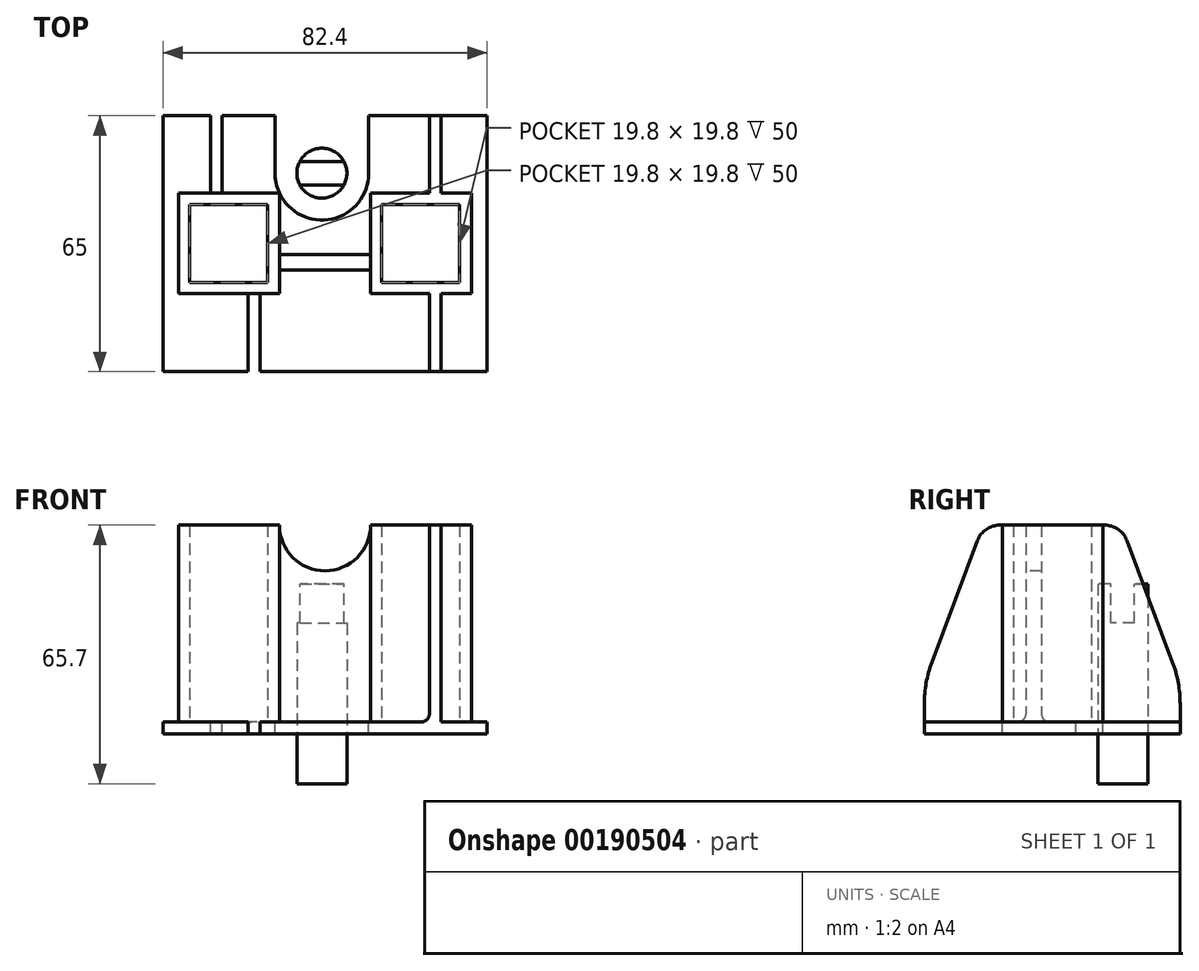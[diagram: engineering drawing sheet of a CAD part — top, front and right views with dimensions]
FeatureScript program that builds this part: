
annotation { "Feature Type Name" : "Feature", "Feature Type Description" : "" }
export const myFeature = defineFeature(function(context is Context, id is Id, definition is map)
    precondition{}
    {
        {
            var Q0;
            Q0=qCreatedBy(makeId("Top.planeOp"),FACE);
            var sketch = newSketch(context, id + "F0", { "sketchPlane" : qUnion([Q0])});
            skLineSegment(sketch, "E0.bottom", {"start": v(-33.6, -8) * mm, "end": v(-13.8, -8) * mm});
            skLineSegment(sketch, "E0.top", {"start": v(-33.6, -27.8) * mm, "end": v(-13.8, -27.8) * mm});
            skLineSegment(sketch, "E0.left", {"start": v(-33.6, -8) * mm, "end": v(-33.6, -27.8) * mm});
            skLineSegment(sketch, "E0.right", {"start": v(-13.8, -8) * mm, "end": v(-13.8, -27.8) * mm});
            skLineSegment(sketch, "E1.bottom", {"start": v(-36.4, -5) * mm, "end": v(-10.8, -5) * mm});
            skLineSegment(sketch, "E1.top", {"start": v(-36.4, -30.6) * mm, "end": v(-10.8, -30.6) * mm});
            skLineSegment(sketch, "E1.left", {"start": v(-36.4, -5) * mm, "end": v(-36.4, -30.6) * mm});
            skLineSegment(sketch, "E1.right", {"start": v(-10.8, -5) * mm, "end": v(-10.8, -30.6) * mm});
            skCircle(sketch, "E2", {"center": v(0, 0) * mm, "radius": 6.35 * mm});
            skLineSegment(sketch, "E3.bottom", {"start": v(15.2, -8) * mm, "end": v(35, -8) * mm});
            skLineSegment(sketch, "E3.top", {"start": v(15.2, -27.8) * mm, "end": v(35, -27.8) * mm});
            skLineSegment(sketch, "E3.left", {"start": v(15.2, -8) * mm, "end": v(15.2, -27.8) * mm});
            skLineSegment(sketch, "E3.right", {"start": v(35, -8) * mm, "end": v(35, -27.8) * mm});
            skLineSegment(sketch, "E4.bottom", {"start": v(12.4, -5) * mm, "end": v(38, -5) * mm});
            skLineSegment(sketch, "E4.top", {"start": v(12.4, -30.6) * mm, "end": v(38, -30.6) * mm});
            skLineSegment(sketch, "E4.left", {"start": v(12.4, -5) * mm, "end": v(12.4, -30.6) * mm});
            skLineSegment(sketch, "E4.right", {"start": v(38, -5) * mm, "end": v(38, -30.6) * mm});
            skLineSegment(sketch, "E5.bottom", {"start": v(42, -50.4) * mm, "end": v(0.8, -50.4) * mm});
            skLineSegment(sketch, "E5.top", {"start": v(42, 14.6) * mm, "end": v(11.9, 14.6) * mm});
            skLineSegment(sketch, "E5.left", {"start": v(42, -50.4) * mm, "end": v(42, 14.6) * mm});
            skLineSegment(sketch, "E5.right", {"start": v(-40.4, -50.4) * mm, "end": v(-40.4, 14.6) * mm});
            skLineSegment(sketch, "E6", {"start": v(9.6, -50.4) * mm, "end": v(-40.4, -50.4) * mm});
            skLineSegment(sketch, "E7", {"start": v(-36.4, -5) * mm, "end": v(-34.4, -5) * mm});
            skArc(sketch, "E8", {"start": v(-11.9, 0) * mm, "mid": v(0, -11.9) * mm, "end": v(11.9, 0) * mm});
            skLineSegment(sketch, "E9", {"start": v(-11.9, 0) * mm, "end": v(-11.9, 14.6) * mm});
            skLineSegment(sketch, "E10", {"start": v(11.9, 0) * mm, "end": v(11.9, 14.6) * mm});
            skLineSegment(sketch, "E11", {"start": v(-11.9, 14.6) * mm, "end": v(-40.4, 14.6) * mm});
            skLineSegment(sketch, "E12.bottom", {"start": v(-18.7, -50.4) * mm, "end": v(-15.7, -50.4) * mm});
            skLineSegment(sketch, "E12.top", {"start": v(-18.7, -30.6) * mm, "end": v(-15.7, -30.6) * mm});
            skLineSegment(sketch, "E12.left", {"start": v(-18.7, -50.4) * mm, "end": v(-18.7, -30.6) * mm});
            skLineSegment(sketch, "E12.right", {"start": v(-15.7, -50.4) * mm, "end": v(-15.7, -30.6) * mm});
            skLineSegment(sketch, "E13.bottom", {"start": v(-28.3, -5) * mm, "end": v(-25.3, -5) * mm});
            skLineSegment(sketch, "E13.top", {"start": v(-28.3, 14.6) * mm, "end": v(-25.3, 14.6) * mm});
            skLineSegment(sketch, "E13.left", {"start": v(-28.3, -5) * mm, "end": v(-28.3, 14.6) * mm});
            skLineSegment(sketch, "E13.right", {"start": v(-25.3, -5) * mm, "end": v(-25.3, 14.6) * mm});
            skLineSegment(sketch, "E14.bottom", {"start": v(-10.8, -20.6) * mm, "end": v(12.4, -20.6) * mm});
            skLineSegment(sketch, "E14.top", {"start": v(-10.8, -24.6) * mm, "end": v(12.4, -24.6) * mm});
            skLineSegment(sketch, "E14.left", {"start": v(-10.8, -20.6) * mm, "end": v(-10.8, -24.6) * mm});
            skLineSegment(sketch, "E14.right", {"start": v(12.4, -20.6) * mm, "end": v(12.4, -24.6) * mm});
            skLineSegment(sketch, "E15.MirrorCS", {"start": v(27.3, -50.4) * mm, "end": v(27.3, -30.6) * mm});
            skLineSegment(sketch, "E16.MirrorCS", {"start": v(30.3, -50.4) * mm, "end": v(30.3, -30.6) * mm});
            skLineSegment(sketch, "E17.MirrorCS", {"start": v(27.3, -5) * mm, "end": v(27.3, 14.6) * mm});
            skLineSegment(sketch, "E18.MirrorCS", {"start": v(30.3, -5) * mm, "end": v(30.3, 14.6) * mm});
            skSolve(sketch);
        }
        {
            var Q0;
            Q0=makeQuery(id+"F0.imprint","IMPRINT",FACE,{"disambiguationData":[TD([[makeQuery(id+"F0.imprint","IMPRINT",EDGE,{"derivedFrom":sQuery(id+"F0.wireOp",EDGE,"E2")}),1.0]])]});
            extrude(context, id + "F1", {"entities" : qUnion([Q0]), "depth" : 50.8 * mm});
        }
        {
            var Q0;
            Q0=makeQuery(id+"F1.opExtrude","CAP_FACE",FACE,{"disambiguationData":[OSD([sQuery(id+"F0.wireOp",EDGE,"E2")])],"isStart":false});
            var sketch = newSketch(context, id + "F2", { "sketchPlane" : qUnion([Q0])});
            skLineSegment(sketch, "E19.bottom", {"start": v(-7.56, 3) * mm, "end": v(-7.56, -3) * mm});
            skLineSegment(sketch, "E19.top", {"start": v(7.56, 3) * mm, "end": v(7.56, -3) * mm});
            skLineSegment(sketch, "E19.left", {"start": v(-7.56, 3) * mm, "end": v(7.56, 3) * mm});
            skLineSegment(sketch, "E19.right", {"start": v(-7.56, -3) * mm, "end": v(7.56, -3) * mm});
            skPoint(sketch, "E19.middle", {"position": v(0, 0) * mm});
            skSolve(sketch);
        }
        {
            var Q0;
            {var subQ0=sQuery(id+"F2.wireOp",EDGE,"E19.left");var subQ1=makeQuery(id+"F1.opExtrude","CAP_EDGE",EDGE,{"disambiguationData":[OSD([sQuery(id+"F0.wireOp",EDGE,"E2")])],"isStart":false});var subQ2=makeQuery(id+"F2.imprint","INTERSECT",VERTEX,{"disambiguationData":[OD(0.0)],"derivedFrom":[subQ1,subQ0]});Q0=makeQuery(id+"F2.imprint","IMPRINT",FACE,{"disambiguationData":[TD([[makeQuery(id+"F2.imprint","IMPRINT",EDGE,{"disambiguationData":[TD([[subQ2,-1.0]])],"derivedFrom":subQ0}),-1.0]])]});}
            extrude(context, id + "F3", {"entities" : qUnion([Q0]), "operationType" : NewBodyOperationType.REMOVE, "oppositeDirection" : true, "depth" : 10 * mm});
        }
        {
            var Q0;
            Q0=makeQuery(id+"F1.opExtrude","SWEPT_BODY",BODY,{"disambiguationData":[OSD([sQuery(id+"F0.wireOp",EDGE,"E2")])]});
            transform(context, id + "F4", {"entities" : qUnion([Q0]), "transformType" : TransformType.TRANSLATION_3D, "dx" : 0 * mm, "dy" : 0 * mm, "dz" : -15.7 * mm, "makeCopy" : false});
        }
        {
            var Q0;
            {var subQ1=sQuery(id+"F0.wireOp",EDGE,"E1.left");Q0=makeQuery(id+"F0.imprint","IMPRINT",FACE,{"disambiguationData":[TD([[makeQuery(id+"F0.imprint","IMPRINT",EDGE,{"derivedFrom":subQ1}),-1.0]])]});}
            var Q1;
            Q1=makeQuery(id+"F0.imprint","IMPRINT",FACE,{"disambiguationData":[TD([[makeQuery(id+"F0.imprint","IMPRINT",EDGE,{"derivedFrom":sQuery(id+"F0.wireOp",EDGE,"E13.bottom")}),1.0]])]});
            var Q2;
            Q2=makeQuery(id+"F0.imprint","IMPRINT",FACE,{"disambiguationData":[TD([[makeQuery(id+"F0.imprint","IMPRINT",EDGE,{"derivedFrom":sQuery(id+"F0.wireOp",EDGE,"E0.bottom")}),1.0]])]});
            var Q3;
            Q3=makeQuery(id+"F0.imprint","IMPRINT",FACE,{"disambiguationData":[TD([[makeQuery(id+"F0.imprint","IMPRINT",EDGE,{"derivedFrom":sQuery(id+"F0.wireOp",EDGE,"E0.bottom")}),-1.0]])]});
            var Q4;
            {var subQ1=sQuery(id+"F0.wireOp",EDGE,"E9");Q4=makeQuery(id+"F0.imprint","IMPRINT",FACE,{"disambiguationData":[TD([[makeQuery(id+"F0.imprint","IMPRINT",EDGE,{"derivedFrom":subQ1}),1.0]])]});}
            var Q5;
            {var subQ0=sQuery(id+"F0.wireOp",EDGE,"E10");Q5=makeQuery(id+"F0.imprint","IMPRINT",FACE,{"disambiguationData":[TD([[makeQuery(id+"F0.imprint","IMPRINT",EDGE,{"derivedFrom":subQ0}),-1.0]])]});}
            var Q6;
            Q6=makeQuery(id+"F0.imprint","IMPRINT",FACE,{"disambiguationData":[TD([[makeQuery(id+"F0.imprint","IMPRINT",EDGE,{"derivedFrom":sQuery(id+"F0.wireOp",EDGE,"E14.bottom")}),-1.0]])]});
            var Q7;
            Q7=makeQuery(id+"F0.imprint","IMPRINT",FACE,{"disambiguationData":[TD([[makeQuery(id+"F0.imprint","IMPRINT",EDGE,{"derivedFrom":sQuery(id+"F0.wireOp",EDGE,"E12.bottom")}),1.0]])]});
            var Q8;
            {var subQ7=sQuery(id+"F0.wireOp",EDGE,"E12.right");Q8=makeQuery(id+"F0.imprint","IMPRINT",FACE,{"disambiguationData":[TD([[makeQuery(id+"F0.imprint","IMPRINT",EDGE,{"derivedFrom":subQ7}),-1.0]])]});}
            var Q9;
            Q9=makeQuery(id+"F0.imprint","IMPRINT",FACE,{"disambiguationData":[TD([[makeQuery(id+"F0.imprint","IMPRINT",EDGE,{"derivedFrom":sQuery(id+"F0.wireOp",EDGE,"E3.bottom")}),1.0]])]});
            var Q10;
            {var subQ0=sQuery(id+"F0.wireOp",EDGE,"E17.MirrorCS");Q10=makeQuery(id+"F0.imprint","IMPRINT",FACE,{"disambiguationData":[TD([[makeQuery(id+"F0.imprint","IMPRINT",EDGE,{"derivedFrom":subQ0}),-1.0]])]});}
            var Q11;
            {var subQ3=sQuery(id+"F0.wireOp",EDGE,"E4.right");Q11=makeQuery(id+"F0.imprint","IMPRINT",FACE,{"disambiguationData":[TD([[makeQuery(id+"F0.imprint","IMPRINT",EDGE,{"derivedFrom":subQ3}),1.0]])]});}
            var Q12;
            {var subQ0=sQuery(id+"F0.wireOp",EDGE,"E15.MirrorCS");Q12=makeQuery(id+"F0.imprint","IMPRINT",FACE,{"disambiguationData":[TD([[makeQuery(id+"F0.imprint","IMPRINT",EDGE,{"derivedFrom":subQ0}),-1.0]])]});}
            var Q13;
            Q13=makeQuery(id+"F0.imprint","IMPRINT",FACE,{"disambiguationData":[TD([[makeQuery(id+"F0.imprint","IMPRINT",EDGE,{"derivedFrom":sQuery(id+"F0.wireOp",EDGE,"E3.bottom")}),-1.0]])]});
            extrude(context, id + "F5", {"entities" : qUnion([Q0, Q1, Q2, Q3, Q4, Q5, Q6, Q7, Q8, Q9, Q10, Q11, Q12, Q13]), "oppositeDirection" : true, "depth" : 3 * mm});
        }
        {
            var Q0;
            Q0=makeQuery(id+"F0.imprint","IMPRINT",FACE,{"disambiguationData":[TD([[makeQuery(id+"F0.imprint","IMPRINT",EDGE,{"derivedFrom":sQuery(id+"F0.wireOp",EDGE,"E0.bottom")}),1.0]])]});
            var Q1;
            Q1=makeQuery(id+"F0.imprint","IMPRINT",FACE,{"disambiguationData":[TD([[makeQuery(id+"F0.imprint","IMPRINT",EDGE,{"derivedFrom":sQuery(id+"F0.wireOp",EDGE,"E3.bottom")}),1.0]])]});
            var Q2;
            Q2=makeQuery(id+"F0.imprint","IMPRINT",FACE,{"disambiguationData":[TD([[makeQuery(id+"F0.imprint","IMPRINT",EDGE,{"derivedFrom":sQuery(id+"F0.wireOp",EDGE,"E14.bottom")}),-1.0]])]});
            var Q3;
            Q3=makeQuery(id+"F0.imprint","IMPRINT",FACE,{"disambiguationData":[TD([[makeQuery(id+"F0.imprint","IMPRINT",EDGE,{"derivedFrom":sQuery(id+"F0.wireOp",EDGE,"E12.bottom")}),1.0]])]});
            var Q4;
            {var subQ0=sQuery(id+"F0.wireOp",EDGE,"E15.MirrorCS");Q4=makeQuery(id+"F0.imprint","IMPRINT",FACE,{"disambiguationData":[TD([[makeQuery(id+"F0.imprint","IMPRINT",EDGE,{"derivedFrom":subQ0}),-1.0]])]});}
            var Q5;
            Q5=makeQuery(id+"F0.imprint","IMPRINT",FACE,{"disambiguationData":[TD([[makeQuery(id+"F0.imprint","IMPRINT",EDGE,{"derivedFrom":sQuery(id+"F0.wireOp",EDGE,"E13.bottom")}),1.0]])]});
            var Q6;
            {var subQ0=sQuery(id+"F0.wireOp",EDGE,"E17.MirrorCS");Q6=makeQuery(id+"F0.imprint","IMPRINT",FACE,{"disambiguationData":[TD([[makeQuery(id+"F0.imprint","IMPRINT",EDGE,{"derivedFrom":subQ0}),-1.0]])]});}
            extrude(context, id + "F6", {"entities" : qUnion([Q0, Q1, Q2, Q3, Q4, Q5, Q6]), "operationType" : NewBodyOperationType.ADD, "depth" : 50 * mm});
        }
        {
            var Q0;
            Q0=makeQuery(id+"F6.opExtrude","SWEPT_FACE",FACE,{"disambiguationData":[OSD([sQuery(id+"F0.wireOp",EDGE,"E14.top")])]});
            var sketch = newSketch(context, id + "F7", { "sketchPlane" : qUnion([Q0])});
            skCircle(sketch, "E20", {"center": v(0.8, 50) * mm, "radius": 11.6 * mm});
            skSolve(sketch);
        }
        {
            var Q0;
            {var subQ1=sQuery(id+"F0.wireOp",EDGE,"E14.top");var subQ2=makeQuery(id+"F6.opExtrude","CAP_EDGE",EDGE,{"disambiguationData":[OSD([subQ1])],"isStart":false});Q0=makeQuery(id+"F7.imprint","IMPRINT",FACE,{"disambiguationData":[TD([[makeQuery(id+"F7.imprint","IMPRINT",EDGE,{"derivedFrom":subQ2}),-1.0]])]});}
            extrude(context, id + "F8", {"entities" : qUnion([Q0]), "operationType" : NewBodyOperationType.REMOVE, "oppositeDirection" : true, "depth" : 4 * mm});
        }
        {
            var Q0;
            Q0=makeQuery(id+"F6.opExtrude","CAP_EDGE",EDGE,{"disambiguationData":[OSD([sQuery(id+"F0.wireOp",EDGE,"E5.bottom")])],"isStart":false});
            var Q1;
            Q1=makeQuery(id+"F6.opExtrude","CAP_EDGE",EDGE,{"disambiguationData":[OSD([sQuery(id+"F0.wireOp",EDGE,"E12.bottom")])],"isStart":false});
            var Q2;
            Q2=makeQuery(id+"F6.opExtrude","CAP_EDGE",EDGE,{"disambiguationData":[OSD([sQuery(id+"F0.wireOp",EDGE,"E5.top")])],"isStart":false});
            var Q3;
            Q3=makeQuery(id+"F6.opExtrude","CAP_EDGE",EDGE,{"disambiguationData":[OSD([sQuery(id+"F0.wireOp",EDGE,"E13.top")])],"isStart":false});
            chamfer(context, id + "F9", {"entities" : qUnion([Q0, Q1, Q2, Q3]), "chamferType" : ChamferType.TWO_OFFSETS, "width1" : 40 * mm, "oppositeDirection" : false, "width2" : 15 * mm, "tangentPropagation" : true});
        }
        {
            var Q0;
            {var subQ0=sQuery(id+"F0.wireOp",EDGE,"E14.top");var subQ1=sQuery(id+"F0.wireOp",EDGE,"E13.right");var subQ2=sQuery(id+"F0.wireOp",EDGE,"E13.left");var subQ3=sQuery(id+"F0.wireOp",EDGE,"E5.bottom");var subQ4=sQuery(id+"F0.wireOp",EDGE,"E13.top");var subQ5=sQuery(id+"F0.wireOp",EDGE,"E12.right");var subQ6=sQuery(id+"F0.wireOp",EDGE,"E12.left");var subQ7=sQuery(id+"F0.wireOp",EDGE,"E14.bottom");var subQ8=sQuery(id+"F0.wireOp",EDGE,"E12.bottom");var subQ9=sQuery(id+"F0.wireOp",EDGE,"E1.right");var subQ10=sQuery(id+"F0.wireOp",EDGE,"E1.bottom");var subQ12=sQuery(id+"F0.wireOp",EDGE,"E0.right");var subQ13=sQuery(id+"F0.wireOp",EDGE,"E1.left");var subQ14=sQuery(id+"F0.wireOp",EDGE,"E0.left");var subQ15=sQuery(id+"F0.wireOp",EDGE,"E1.top");var subQ17=sQuery(id+"F0.wireOp",EDGE,"E0.top");var subQ18=sQuery(id+"F0.wireOp",EDGE,"E0.bottom");var subQ19=sQuery(id+"F0.wireOp",EDGE,"E7");Q0=makeQuery(id+"F9.opChamfer","BLEND_EDGE",EDGE,{"blendedFrom":[makeQuery(id+"F6.opExtrude","CAP_EDGE",EDGE,{"disambiguationData":[OSD([subQ8])],"isStart":false}),makeQuery(id+"F8.boolean.opBoolean","SPLIT",FACE,{"disambiguationData":[TD([makeQuery(id+"F6.opExtrude","SWEPT_FACE",FACE,{"disambiguationData":[OSD([subQ18])]})])],"derivedFrom":makeQuery(id+"F6.opExtrude","CAP_FACE",FACE,{"disambiguationData":[OSD([subQ18,subQ17,subQ14,subQ12,subQ10,subQ15,subQ13,subQ9,sQuery(id+"F0.wireOp",EDGE,"E3.bottom"),sQuery(id+"F0.wireOp",EDGE,"E3.top"),sQuery(id+"F0.wireOp",EDGE,"E3.left"),sQuery(id+"F0.wireOp",EDGE,"E3.right"),sQuery(id+"F0.wireOp",EDGE,"E4.bottom"),sQuery(id+"F0.wireOp",EDGE,"E4.top"),sQuery(id+"F0.wireOp",EDGE,"E4.left"),sQuery(id+"F0.wireOp",EDGE,"E4.right"),subQ3,sQuery(id+"F0.wireOp",EDGE,"E5.top"),subQ19,subQ8,subQ6,subQ5,subQ4,subQ2,subQ1,subQ7,subQ0,sQuery(id+"F0.wireOp",EDGE,"E15.MirrorCS"),sQuery(id+"F0.wireOp",EDGE,"E16.MirrorCS"),sQuery(id+"F0.wireOp",EDGE,"E17.MirrorCS"),sQuery(id+"F0.wireOp",EDGE,"E18.MirrorCS")])],"isStart":false})})],"blendedInto":[makeQuery(id+"F8.boolean.opBoolean","SPLIT",FACE,{"disambiguationData":[TD([makeQuery(id+"F6.opExtrude","SWEPT_FACE",FACE,{"disambiguationData":[OSD([subQ18])]})])],"derivedFrom":makeQuery(id+"F6.opExtrude","CAP_FACE",FACE,{"disambiguationData":[OSD([subQ18,subQ17,subQ14,subQ12,subQ10,subQ15,subQ13,subQ9,sQuery(id+"F0.wireOp",EDGE,"E3.bottom"),sQuery(id+"F0.wireOp",EDGE,"E3.top"),sQuery(id+"F0.wireOp",EDGE,"E3.left"),sQuery(id+"F0.wireOp",EDGE,"E3.right"),sQuery(id+"F0.wireOp",EDGE,"E4.bottom"),sQuery(id+"F0.wireOp",EDGE,"E4.top"),sQuery(id+"F0.wireOp",EDGE,"E4.left"),sQuery(id+"F0.wireOp",EDGE,"E4.right"),subQ3,sQuery(id+"F0.wireOp",EDGE,"E5.top"),subQ19,subQ8,subQ6,subQ5,subQ4,subQ2,subQ1,subQ7,subQ0,sQuery(id+"F0.wireOp",EDGE,"E15.MirrorCS"),sQuery(id+"F0.wireOp",EDGE,"E16.MirrorCS"),sQuery(id+"F0.wireOp",EDGE,"E17.MirrorCS"),sQuery(id+"F0.wireOp",EDGE,"E18.MirrorCS")])],"isStart":false})})]});}
            var Q1;
            {var subQ0=sQuery(id+"F0.wireOp",EDGE,"E16.MirrorCS");var subQ1=sQuery(id+"F0.wireOp",EDGE,"E15.MirrorCS");var subQ2=sQuery(id+"F0.wireOp",EDGE,"E12.bottom");var subQ3=sQuery(id+"F0.wireOp",EDGE,"E5.bottom");var subQ4=sQuery(id+"F0.wireOp",EDGE,"E3.bottom");var subQ5=sQuery(id+"F0.wireOp",EDGE,"E14.top");var subQ6=sQuery(id+"F0.wireOp",EDGE,"E14.bottom");var subQ7=sQuery(id+"F0.wireOp",EDGE,"E4.right");var subQ8=sQuery(id+"F0.wireOp",EDGE,"E4.top");var subQ9=sQuery(id+"F0.wireOp",EDGE,"E5.top");var subQ10=sQuery(id+"F0.wireOp",EDGE,"E4.left");var subQ13=sQuery(id+"F0.wireOp",EDGE,"E3.right");var subQ14=sQuery(id+"F0.wireOp",EDGE,"E3.top");var subQ15=sQuery(id+"F0.wireOp",EDGE,"E18.MirrorCS");var subQ16=sQuery(id+"F0.wireOp",EDGE,"E4.bottom");var subQ18=sQuery(id+"F0.wireOp",EDGE,"E17.MirrorCS");var subQ19=sQuery(id+"F0.wireOp",EDGE,"E3.left");Q1=makeQuery(id+"F9.opChamfer","BLEND_EDGE",EDGE,{"blendedFrom":[makeQuery(id+"F6.opExtrude","CAP_EDGE",EDGE,{"disambiguationData":[OSD([subQ3])],"isStart":false}),makeQuery(id+"F8.boolean.opBoolean","SPLIT",FACE,{"disambiguationData":[TD([makeQuery(id+"F5.opExtrude","SWEPT_FACE",FACE,{"disambiguationData":[OSD([subQ9])]})])],"derivedFrom":makeQuery(id+"F6.opExtrude","CAP_FACE",FACE,{"disambiguationData":[OSD([sQuery(id+"F0.wireOp",EDGE,"E0.bottom"),sQuery(id+"F0.wireOp",EDGE,"E0.top"),sQuery(id+"F0.wireOp",EDGE,"E0.left"),sQuery(id+"F0.wireOp",EDGE,"E0.right"),sQuery(id+"F0.wireOp",EDGE,"E1.bottom"),sQuery(id+"F0.wireOp",EDGE,"E1.top"),sQuery(id+"F0.wireOp",EDGE,"E1.left"),sQuery(id+"F0.wireOp",EDGE,"E1.right"),subQ4,subQ14,subQ19,subQ13,subQ16,subQ8,subQ10,subQ7,subQ3,subQ9,sQuery(id+"F0.wireOp",EDGE,"E7"),subQ2,sQuery(id+"F0.wireOp",EDGE,"E12.left"),sQuery(id+"F0.wireOp",EDGE,"E12.right"),sQuery(id+"F0.wireOp",EDGE,"E13.top"),sQuery(id+"F0.wireOp",EDGE,"E13.left"),sQuery(id+"F0.wireOp",EDGE,"E13.right"),subQ6,subQ5,subQ1,subQ0,subQ18,subQ15])],"isStart":false})})],"blendedInto":[makeQuery(id+"F8.boolean.opBoolean","SPLIT",FACE,{"disambiguationData":[TD([makeQuery(id+"F5.opExtrude","SWEPT_FACE",FACE,{"disambiguationData":[OSD([subQ9])]})])],"derivedFrom":makeQuery(id+"F6.opExtrude","CAP_FACE",FACE,{"disambiguationData":[OSD([sQuery(id+"F0.wireOp",EDGE,"E0.bottom"),sQuery(id+"F0.wireOp",EDGE,"E0.top"),sQuery(id+"F0.wireOp",EDGE,"E0.left"),sQuery(id+"F0.wireOp",EDGE,"E0.right"),sQuery(id+"F0.wireOp",EDGE,"E1.bottom"),sQuery(id+"F0.wireOp",EDGE,"E1.top"),sQuery(id+"F0.wireOp",EDGE,"E1.left"),sQuery(id+"F0.wireOp",EDGE,"E1.right"),subQ4,subQ14,subQ19,subQ13,subQ16,subQ8,subQ10,subQ7,subQ3,subQ9,sQuery(id+"F0.wireOp",EDGE,"E7"),subQ2,sQuery(id+"F0.wireOp",EDGE,"E12.left"),sQuery(id+"F0.wireOp",EDGE,"E12.right"),sQuery(id+"F0.wireOp",EDGE,"E13.top"),sQuery(id+"F0.wireOp",EDGE,"E13.left"),sQuery(id+"F0.wireOp",EDGE,"E13.right"),subQ6,subQ5,subQ1,subQ0,subQ18,subQ15])],"isStart":false})})]});}
            var Q2;
            {var subQ0=sQuery(id+"F0.wireOp",EDGE,"E16.MirrorCS");var subQ1=sQuery(id+"F0.wireOp",EDGE,"E15.MirrorCS");var subQ2=sQuery(id+"F0.wireOp",EDGE,"E12.bottom");var subQ3=sQuery(id+"F0.wireOp",EDGE,"E5.bottom");var subQ4=sQuery(id+"F0.wireOp",EDGE,"E3.bottom");var subQ5=sQuery(id+"F0.wireOp",EDGE,"E14.top");var subQ6=sQuery(id+"F0.wireOp",EDGE,"E14.bottom");var subQ7=sQuery(id+"F0.wireOp",EDGE,"E4.right");var subQ8=sQuery(id+"F0.wireOp",EDGE,"E4.top");var subQ9=sQuery(id+"F0.wireOp",EDGE,"E5.top");var subQ10=sQuery(id+"F0.wireOp",EDGE,"E4.left");var subQ13=sQuery(id+"F0.wireOp",EDGE,"E3.right");var subQ14=sQuery(id+"F0.wireOp",EDGE,"E3.top");var subQ15=sQuery(id+"F0.wireOp",EDGE,"E18.MirrorCS");var subQ16=sQuery(id+"F0.wireOp",EDGE,"E4.bottom");var subQ18=sQuery(id+"F0.wireOp",EDGE,"E17.MirrorCS");var subQ19=sQuery(id+"F0.wireOp",EDGE,"E3.left");Q2=makeQuery(id+"F9.opChamfer","BLEND_EDGE",EDGE,{"blendedFrom":[makeQuery(id+"F6.opExtrude","CAP_EDGE",EDGE,{"disambiguationData":[OSD([subQ9])],"isStart":false}),makeQuery(id+"F8.boolean.opBoolean","SPLIT",FACE,{"disambiguationData":[TD([makeQuery(id+"F5.opExtrude","SWEPT_FACE",FACE,{"disambiguationData":[OSD([subQ9])]})])],"derivedFrom":makeQuery(id+"F6.opExtrude","CAP_FACE",FACE,{"disambiguationData":[OSD([sQuery(id+"F0.wireOp",EDGE,"E0.bottom"),sQuery(id+"F0.wireOp",EDGE,"E0.top"),sQuery(id+"F0.wireOp",EDGE,"E0.left"),sQuery(id+"F0.wireOp",EDGE,"E0.right"),sQuery(id+"F0.wireOp",EDGE,"E1.bottom"),sQuery(id+"F0.wireOp",EDGE,"E1.top"),sQuery(id+"F0.wireOp",EDGE,"E1.left"),sQuery(id+"F0.wireOp",EDGE,"E1.right"),subQ4,subQ14,subQ19,subQ13,subQ16,subQ8,subQ10,subQ7,subQ3,subQ9,sQuery(id+"F0.wireOp",EDGE,"E7"),subQ2,sQuery(id+"F0.wireOp",EDGE,"E12.left"),sQuery(id+"F0.wireOp",EDGE,"E12.right"),sQuery(id+"F0.wireOp",EDGE,"E13.top"),sQuery(id+"F0.wireOp",EDGE,"E13.left"),sQuery(id+"F0.wireOp",EDGE,"E13.right"),subQ6,subQ5,subQ1,subQ0,subQ18,subQ15])],"isStart":false})})],"blendedInto":[makeQuery(id+"F8.boolean.opBoolean","SPLIT",FACE,{"disambiguationData":[TD([makeQuery(id+"F5.opExtrude","SWEPT_FACE",FACE,{"disambiguationData":[OSD([subQ9])]})])],"derivedFrom":makeQuery(id+"F6.opExtrude","CAP_FACE",FACE,{"disambiguationData":[OSD([sQuery(id+"F0.wireOp",EDGE,"E0.bottom"),sQuery(id+"F0.wireOp",EDGE,"E0.top"),sQuery(id+"F0.wireOp",EDGE,"E0.left"),sQuery(id+"F0.wireOp",EDGE,"E0.right"),sQuery(id+"F0.wireOp",EDGE,"E1.bottom"),sQuery(id+"F0.wireOp",EDGE,"E1.top"),sQuery(id+"F0.wireOp",EDGE,"E1.left"),sQuery(id+"F0.wireOp",EDGE,"E1.right"),subQ4,subQ14,subQ19,subQ13,subQ16,subQ8,subQ10,subQ7,subQ3,subQ9,sQuery(id+"F0.wireOp",EDGE,"E7"),subQ2,sQuery(id+"F0.wireOp",EDGE,"E12.left"),sQuery(id+"F0.wireOp",EDGE,"E12.right"),sQuery(id+"F0.wireOp",EDGE,"E13.top"),sQuery(id+"F0.wireOp",EDGE,"E13.left"),sQuery(id+"F0.wireOp",EDGE,"E13.right"),subQ6,subQ5,subQ1,subQ0,subQ18,subQ15])],"isStart":false})})]});}
            var Q3;
            {var subQ0=sQuery(id+"F0.wireOp",EDGE,"E14.top");var subQ1=sQuery(id+"F0.wireOp",EDGE,"E13.right");var subQ2=sQuery(id+"F0.wireOp",EDGE,"E13.left");var subQ3=sQuery(id+"F0.wireOp",EDGE,"E5.bottom");var subQ4=sQuery(id+"F0.wireOp",EDGE,"E13.top");var subQ5=sQuery(id+"F0.wireOp",EDGE,"E12.right");var subQ6=sQuery(id+"F0.wireOp",EDGE,"E12.left");var subQ7=sQuery(id+"F0.wireOp",EDGE,"E14.bottom");var subQ8=sQuery(id+"F0.wireOp",EDGE,"E12.bottom");var subQ9=sQuery(id+"F0.wireOp",EDGE,"E1.right");var subQ10=sQuery(id+"F0.wireOp",EDGE,"E1.bottom");var subQ12=sQuery(id+"F0.wireOp",EDGE,"E0.right");var subQ13=sQuery(id+"F0.wireOp",EDGE,"E1.left");var subQ14=sQuery(id+"F0.wireOp",EDGE,"E0.left");var subQ15=sQuery(id+"F0.wireOp",EDGE,"E1.top");var subQ17=sQuery(id+"F0.wireOp",EDGE,"E0.top");var subQ18=sQuery(id+"F0.wireOp",EDGE,"E0.bottom");var subQ19=sQuery(id+"F0.wireOp",EDGE,"E7");Q3=makeQuery(id+"F9.opChamfer","BLEND_EDGE",EDGE,{"blendedFrom":[makeQuery(id+"F6.opExtrude","CAP_EDGE",EDGE,{"disambiguationData":[OSD([subQ4])],"isStart":false}),makeQuery(id+"F8.boolean.opBoolean","SPLIT",FACE,{"disambiguationData":[TD([makeQuery(id+"F6.opExtrude","SWEPT_FACE",FACE,{"disambiguationData":[OSD([subQ18])]})])],"derivedFrom":makeQuery(id+"F6.opExtrude","CAP_FACE",FACE,{"disambiguationData":[OSD([subQ18,subQ17,subQ14,subQ12,subQ10,subQ15,subQ13,subQ9,sQuery(id+"F0.wireOp",EDGE,"E3.bottom"),sQuery(id+"F0.wireOp",EDGE,"E3.top"),sQuery(id+"F0.wireOp",EDGE,"E3.left"),sQuery(id+"F0.wireOp",EDGE,"E3.right"),sQuery(id+"F0.wireOp",EDGE,"E4.bottom"),sQuery(id+"F0.wireOp",EDGE,"E4.top"),sQuery(id+"F0.wireOp",EDGE,"E4.left"),sQuery(id+"F0.wireOp",EDGE,"E4.right"),subQ3,sQuery(id+"F0.wireOp",EDGE,"E5.top"),subQ19,subQ8,subQ6,subQ5,subQ4,subQ2,subQ1,subQ7,subQ0,sQuery(id+"F0.wireOp",EDGE,"E15.MirrorCS"),sQuery(id+"F0.wireOp",EDGE,"E16.MirrorCS"),sQuery(id+"F0.wireOp",EDGE,"E17.MirrorCS"),sQuery(id+"F0.wireOp",EDGE,"E18.MirrorCS")])],"isStart":false})})],"blendedInto":[makeQuery(id+"F8.boolean.opBoolean","SPLIT",FACE,{"disambiguationData":[TD([makeQuery(id+"F6.opExtrude","SWEPT_FACE",FACE,{"disambiguationData":[OSD([subQ18])]})])],"derivedFrom":makeQuery(id+"F6.opExtrude","CAP_FACE",FACE,{"disambiguationData":[OSD([subQ18,subQ17,subQ14,subQ12,subQ10,subQ15,subQ13,subQ9,sQuery(id+"F0.wireOp",EDGE,"E3.bottom"),sQuery(id+"F0.wireOp",EDGE,"E3.top"),sQuery(id+"F0.wireOp",EDGE,"E3.left"),sQuery(id+"F0.wireOp",EDGE,"E3.right"),sQuery(id+"F0.wireOp",EDGE,"E4.bottom"),sQuery(id+"F0.wireOp",EDGE,"E4.top"),sQuery(id+"F0.wireOp",EDGE,"E4.left"),sQuery(id+"F0.wireOp",EDGE,"E4.right"),subQ3,sQuery(id+"F0.wireOp",EDGE,"E5.top"),subQ19,subQ8,subQ6,subQ5,subQ4,subQ2,subQ1,subQ7,subQ0,sQuery(id+"F0.wireOp",EDGE,"E15.MirrorCS"),sQuery(id+"F0.wireOp",EDGE,"E16.MirrorCS"),sQuery(id+"F0.wireOp",EDGE,"E17.MirrorCS"),sQuery(id+"F0.wireOp",EDGE,"E18.MirrorCS")])],"isStart":false})})]});}
            fillet(context, id + "F10", {"entities" : qUnion([Q0, Q1, Q2, Q3]), "radius" : 6 * mm, "tangentPropagation" : true, "allowEdgeOverflow" : false});
        }
        {
            var Q0;
            {var subQ0=sQuery(id+"F0.wireOp",EDGE,"E12.bottom");var subQ1=sQuery(id+"F0.wireOp",EDGE,"E5.bottom");Q0=makeQuery(id+"F9.opChamfer","BLEND_EDGE",EDGE,{"blendedFrom":[makeQuery(id+"F6.opExtrude","CAP_EDGE",EDGE,{"disambiguationData":[OSD([subQ0])],"isStart":false}),makeQuery(id+"F6.boolean.opBoolean","MERGE",FACE,{"derivedFrom":[makeQuery(id+"F5.opExtrude","SWEPT_FACE",FACE,{"disambiguationData":[OSD([subQ1,sQuery(id+"F0.wireOp",EDGE,"E6"),subQ0])]}),makeQuery(id+"F6.opExtrude","SWEPT_FACE",FACE,{"disambiguationData":[OSD([subQ1])]}),makeQuery(id+"F6.opExtrude","SWEPT_FACE",FACE,{"disambiguationData":[OSD([subQ0])]})]})],"blendedInto":[makeQuery(id+"F6.boolean.opBoolean","MERGE",FACE,{"derivedFrom":[makeQuery(id+"F5.opExtrude","SWEPT_FACE",FACE,{"disambiguationData":[OSD([subQ1,sQuery(id+"F0.wireOp",EDGE,"E6"),subQ0])]}),makeQuery(id+"F6.opExtrude","SWEPT_FACE",FACE,{"disambiguationData":[OSD([subQ1])]}),makeQuery(id+"F6.opExtrude","SWEPT_FACE",FACE,{"disambiguationData":[OSD([subQ0])]})]})]});}
            var Q1;
            {var subQ0=sQuery(id+"F0.wireOp",EDGE,"E12.bottom");var subQ1=sQuery(id+"F0.wireOp",EDGE,"E5.bottom");Q1=makeQuery(id+"F9.opChamfer","BLEND_EDGE",EDGE,{"blendedFrom":[makeQuery(id+"F6.opExtrude","CAP_EDGE",EDGE,{"disambiguationData":[OSD([subQ1])],"isStart":false}),makeQuery(id+"F6.boolean.opBoolean","MERGE",FACE,{"derivedFrom":[makeQuery(id+"F5.opExtrude","SWEPT_FACE",FACE,{"disambiguationData":[OSD([subQ1,sQuery(id+"F0.wireOp",EDGE,"E6"),subQ0])]}),makeQuery(id+"F6.opExtrude","SWEPT_FACE",FACE,{"disambiguationData":[OSD([subQ1])]}),makeQuery(id+"F6.opExtrude","SWEPT_FACE",FACE,{"disambiguationData":[OSD([subQ0])]})]})],"blendedInto":[makeQuery(id+"F6.boolean.opBoolean","MERGE",FACE,{"derivedFrom":[makeQuery(id+"F5.opExtrude","SWEPT_FACE",FACE,{"disambiguationData":[OSD([subQ1,sQuery(id+"F0.wireOp",EDGE,"E6"),subQ0])]}),makeQuery(id+"F6.opExtrude","SWEPT_FACE",FACE,{"disambiguationData":[OSD([subQ1])]}),makeQuery(id+"F6.opExtrude","SWEPT_FACE",FACE,{"disambiguationData":[OSD([subQ0])]})]})]});}
            var Q2;
            {var subQ0=sQuery(id+"F0.wireOp",EDGE,"E5.top");Q2=makeQuery(id+"F9.opChamfer","BLEND_EDGE",EDGE,{"blendedFrom":[makeQuery(id+"F6.opExtrude","CAP_EDGE",EDGE,{"disambiguationData":[OSD([subQ0])],"isStart":false}),makeQuery(id+"F6.boolean.opBoolean","MERGE",FACE,{"derivedFrom":[makeQuery(id+"F5.opExtrude","SWEPT_FACE",FACE,{"disambiguationData":[OSD([subQ0])]}),makeQuery(id+"F6.opExtrude","SWEPT_FACE",FACE,{"disambiguationData":[OSD([subQ0])]})]})],"blendedInto":[makeQuery(id+"F6.boolean.opBoolean","MERGE",FACE,{"derivedFrom":[makeQuery(id+"F5.opExtrude","SWEPT_FACE",FACE,{"disambiguationData":[OSD([subQ0])]}),makeQuery(id+"F6.opExtrude","SWEPT_FACE",FACE,{"disambiguationData":[OSD([subQ0])]})]})]});}
            var Q3;
            {var subQ0=sQuery(id+"F0.wireOp",EDGE,"E13.top");Q3=makeQuery(id+"F9.opChamfer","BLEND_EDGE",EDGE,{"blendedFrom":[makeQuery(id+"F6.opExtrude","CAP_EDGE",EDGE,{"disambiguationData":[OSD([subQ0])],"isStart":false}),makeQuery(id+"F6.boolean.opBoolean","MERGE",FACE,{"derivedFrom":[makeQuery(id+"F5.opExtrude","SWEPT_FACE",FACE,{"disambiguationData":[OSD([sQuery(id+"F0.wireOp",EDGE,"E11"),subQ0])]}),makeQuery(id+"F6.opExtrude","SWEPT_FACE",FACE,{"disambiguationData":[OSD([subQ0])]})]})],"blendedInto":[makeQuery(id+"F6.boolean.opBoolean","MERGE",FACE,{"derivedFrom":[makeQuery(id+"F5.opExtrude","SWEPT_FACE",FACE,{"disambiguationData":[OSD([sQuery(id+"F0.wireOp",EDGE,"E11"),subQ0])]}),makeQuery(id+"F6.opExtrude","SWEPT_FACE",FACE,{"disambiguationData":[OSD([subQ0])]})]})]});}
            fillet(context, id + "F11", {"entities" : qUnion([Q0, Q1, Q2, Q3]), "radius" : 30 * mm, "tangentPropagation" : true, "allowEdgeOverflow" : false});
        }
        {
            var Q0;
            Q0=makeQuery(id+"F6.opExtrude","CAP_EDGE",EDGE,{"disambiguationData":[OSD([sQuery(id+"F0.wireOp",EDGE,"E17.MirrorCS")])],"isStart":true});
            var Q1;
            Q1=makeQuery(id+"F6.opExtrude","CAP_EDGE",EDGE,{"disambiguationData":[OSD([sQuery(id+"F0.wireOp",EDGE,"E14.bottom")])],"isStart":true});
            var Q2;
            Q2=makeQuery(id+"F6.opExtrude","CAP_EDGE",EDGE,{"disambiguationData":[OSD([sQuery(id+"F0.wireOp",EDGE,"E13.left")])],"isStart":true});
            var Q3;
            Q3=makeQuery(id+"F6.opExtrude","CAP_EDGE",EDGE,{"disambiguationData":[OSD([sQuery(id+"F0.wireOp",EDGE,"E13.right")])],"isStart":true});
            var Q4;
            Q4=makeQuery(id+"F6.opExtrude","CAP_EDGE",EDGE,{"disambiguationData":[OSD([sQuery(id+"F0.wireOp",EDGE,"E18.MirrorCS")])],"isStart":true});
            var Q5;
            Q5=makeQuery(id+"F6.opExtrude","CAP_EDGE",EDGE,{"disambiguationData":[OSD([sQuery(id+"F0.wireOp",EDGE,"E14.top")])],"isStart":true});
            var Q6;
            Q6=makeQuery(id+"F6.opExtrude","CAP_EDGE",EDGE,{"disambiguationData":[OSD([sQuery(id+"F0.wireOp",EDGE,"E12.right")])],"isStart":true});
            var Q7;
            Q7=makeQuery(id+"F6.opExtrude","CAP_EDGE",EDGE,{"disambiguationData":[OSD([sQuery(id+"F0.wireOp",EDGE,"E12.left")])],"isStart":true});
            var Q8;
            Q8=makeQuery(id+"F6.opExtrude","CAP_EDGE",EDGE,{"disambiguationData":[OSD([sQuery(id+"F0.wireOp",EDGE,"E16.MirrorCS")])],"isStart":true});
            var Q9;
            Q9=makeQuery(id+"F6.opExtrude","CAP_EDGE",EDGE,{"disambiguationData":[OSD([sQuery(id+"F0.wireOp",EDGE,"E15.MirrorCS")])],"isStart":true});
            fillet(context, id + "F12", {"entities" : qUnion([Q0, Q1, Q2, Q3, Q4, Q5, Q6, Q7, Q8, Q9]), "radius" : 2 * mm, "tangentPropagation" : true, "allowEdgeOverflow" : false});
        }
    });
